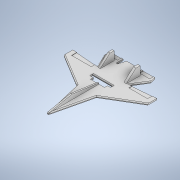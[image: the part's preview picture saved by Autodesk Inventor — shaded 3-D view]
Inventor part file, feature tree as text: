
AUTODESK INVENTOR PART (.ipt)
format: ipt  version: 2020 (Build 240168000, 168)  size: 264,704 bytes
history: native  units: in
note: dims shown in document units (in); Inventor stores cm internally (conversion verified against a paired STEP export)
features: extrude x14, sketch x12, fillet x2
ambient origin geometry x8: Origin, YZ Plane, XZ Plane, XY Plane, X Axis, Y Axis, Z Axis, Center Point
bodies: Solid1 (feature_tree)
feature tree (28):
  sketch  "Sketch1"  dims[d0=12.0in d1=0.2in]
  extrude  "Extrusion1"  Depth=0.2in
  extrude  "Extrusion2"  Depth=0.2in TaperAngle=0.0deg
  extrude  "Extrusion3"  Depth=4.0in TaperAngle=0.0deg
  sketch  "Sketch2"  dims[d2=12.0in d3=0.0in d4=0.2in d5=0.0in]
  extrude  "Extrusion4"  Depth=4.0in TaperAngle=0.0deg
  sketch  "Sketch4"  dims[d10=4.0in d11=0.0in d12=4.0in d13=0.0in]
  extrude  "Extrusion5"  Depth=4.0in TaperAngle=0.0deg
  extrude  "Extrusion6"  Depth=4.0in
  extrude  "Extrusion7"  Depth=0.125in
  extrude  "Extrusion8"  Depth=0.05in TaperAngle=0.0deg
  extrude  "Extrusion9"  Depth=0.05in TaperAngle=0.0deg
  extrude  "Extrusion10"  [1 undecoded]
  sketch  "Sketch9"  dims[d27=0.05in d28=0.0in d29=0.05in d30=0.0in]
  fillet  "Fillet1"  [1 undecoded]
  fillet  "Fillet2"  [1 undecoded]
  sketch  "Sketch10"  dims[d31=0.05in d32=0.0in]
  sketch  "Sketch11"
  extrude  "Extrusion11"  [1 undecoded]
  extrude  "Extrusion12"  [1 undecoded]
  sketch  "Sketch12"
  extrude  "Extrusion13"  [1 undecoded]
  extrude  "Extrusion14"  [1 undecoded]
  sketch  "Sketch3"  dims[d6=4.0in d7=0.0in d8=4.0in d9=0.0in]
  sketch  "Sketch5"  dims[d14=4.0in d15=0.0in d16=4.0in d17=0.0in]
  sketch  "Sketch6"  dims[d18=4.0in d19=0.0in d20=4.0in]
  sketch  "Sketch7"  dims[d21=4.0in d22=0.0in d23=0.125in]
  sketch  "Sketch8"  dims[d24=0.125in d25=0.05in d26=0.0in]
note: 7 required parameter values undecoded (feature->parameter linkage not recoverable at this tier; creation-order binding heuristic only, values carry confidence <= 0.55)
